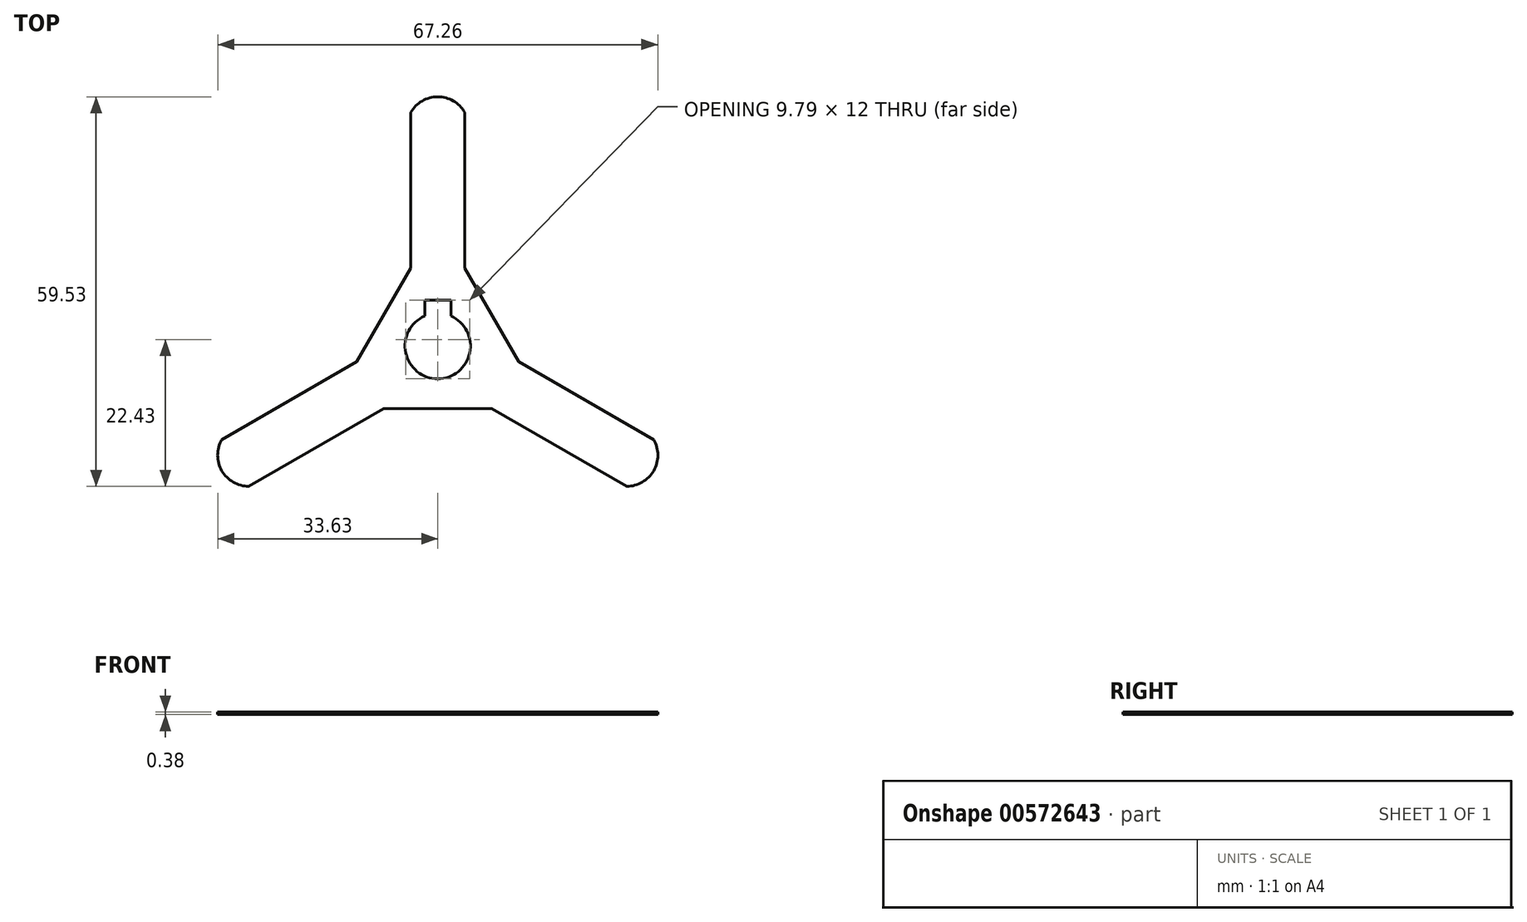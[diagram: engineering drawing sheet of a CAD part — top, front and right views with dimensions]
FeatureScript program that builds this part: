
annotation { "Feature Type Name" : "Feature", "Feature Type Description" : "" }
export const myFeature = defineFeature(function(context is Context, id is Id, definition is map)
    precondition{}
    {
        {
            assignVariable(context, id + "F0", {"name" : "AT", "anyValue" : 3 / 8});
        }
        {
            var Q0;
            Q0=qCreatedBy(makeId("Top.planeOp"),FACE);
            var sketch = newSketch(context, id + "F1", { "sketchPlane" : qUnion([Q0])});
            skCircle(sketch, "E0.cCircle", {"center": v(0, 0) * mm, "radius": 42.86 * mm, "construction": true});
            skLineSegment(sketch, "E0.0", {"start": v(4.12, 35.72) * mm, "end": v(33, -14.29) * mm});
            skLineSegment(sketch, "E0.1", {"start": v(28.87, -21.43) * mm, "end": v(-28.87, -21.43) * mm});
            skLineSegment(sketch, "E0.2", {"start": v(-33, -14.29) * mm, "end": v(-4.12, 35.72) * mm});
            skPoint(sketch, "E1.visualSharp", {"position": v(0, 42.86) * mm});
            skArc(sketch, "E1.filletArc", {"start": v(4.12, 35.72) * mm, "mid": v(0, 38.1) * mm, "end": v(-4.12, 35.72) * mm});
            skPoint(sketch, "E2.visualSharp", {"position": v(37.12, -21.43) * mm});
            skArc(sketch, "E2.filletArc", {"start": v(28.87, -21.43) * mm, "mid": v(33, -19.05) * mm, "end": v(33, -14.29) * mm});
            skPoint(sketch, "E3.visualSharp", {"position": v(-37.12, -21.43) * mm});
            skArc(sketch, "E3.filletArc", {"start": v(-33, -14.29) * mm, "mid": v(-33, -19.05) * mm, "end": v(-28.87, -21.43) * mm});
            skPoint(sketch, "E4", {"position": v(-8.25, 0) * mm});
            skPoint(sketch, "E5", {"position": v(8.25, 0) * mm});
            skPoint(sketch, "E6", {"position": v(-4.12, -7.14) * mm});
            skPoint(sketch, "E7", {"position": v(4.12, -7.14) * mm});
            skPoint(sketch, "E8", {"position": v(4.12, 7.14) * mm});
            skPoint(sketch, "E9", {"position": v(-4.12, 7.14) * mm});
            skLineSegment(sketch, "E10", {"start": v(-28.87, -21.43) * mm, "end": v(-4.12, -7.14) * mm});
            skLineSegment(sketch, "E11", {"start": v(-33, -14.29) * mm, "end": v(-8.25, 0) * mm});
            skLineSegment(sketch, "E12", {"start": v(-4.12, 35.72) * mm, "end": v(-4.12, 7.14) * mm});
            skLineSegment(sketch, "E13", {"start": v(4.12, 7.14) * mm, "end": v(4.12, 35.72) * mm});
            skLineSegment(sketch, "E14", {"start": v(8.25, 0) * mm, "end": v(33, -14.29) * mm});
            skLineSegment(sketch, "E15", {"start": v(28.87, -21.43) * mm, "end": v(4.12, -7.14) * mm});
            skLineSegment(sketch, "E16", {"start": v(4.12, -7.14) * mm, "end": v(-4.12, -7.14) * mm});
            skLineSegment(sketch, "E17", {"start": v(-8.25, 0) * mm, "end": v(-4.12, 7.14) * mm});
            skLineSegment(sketch, "E18", {"start": v(4.12, 7.14) * mm, "end": v(8.25, 0) * mm});
            skCircle(sketch, "E19", {"center": v(0, 0) * mm, "radius": 5 * mm});
            skLineSegment(sketch, "E20", {"start": v(0, 5) * mm, "end": v(0, 3) * mm});
            skLineSegment(sketch, "E21", {"start": v(0, 3) * mm, "end": v(2, 3) * mm});
            skLineSegment(sketch, "E22", {"start": v(0, 3) * mm, "end": v(-2, 3) * mm});
            skLineSegment(sketch, "E23", {"start": v(-2, 3) * mm, "end": v(-2, 7) * mm});
            skLineSegment(sketch, "E24", {"start": v(-2, 7) * mm, "end": v(2, 7) * mm});
            skLineSegment(sketch, "E25", {"start": v(2, 7) * mm, "end": v(2, 3) * mm});
            skPoint(sketch, "E26", {"position": v(0, 5) * mm});
            skLineSegment(sketch, "E27", {"start": v(-2, 7) * mm, "end": v(2, 3) * mm});
            skLineSegment(sketch, "E28", {"start": v(0, 0) * mm, "end": v(0, 19.05) * mm});
            skLineSegment(sketch, "E29", {"start": v(0, 0) * mm, "end": v(16.5, -9.52) * mm});
            skLineSegment(sketch, "E30", {"start": v(0, 0) * mm, "end": v(-16.5, -9.52) * mm});
            skLineSegment(sketch, "E31", {"start": v(-16.5, -9.52) * mm, "end": v(0, 19.05) * mm});
            skLineSegment(sketch, "E32", {"start": v(16.5, -9.53) * mm, "end": v(0, 19.05) * mm});
            skLineSegment(sketch, "E33", {"start": v(-16.5, -9.52) * mm, "end": v(16.5, -9.52) * mm});
            skSolve(sketch);
        }
        {
            var Q0;
            Q0=makeQuery(id+"F1.imprint","IMPRINT",FACE,{"disambiguationData":[TD([[makeQuery(id+"F1.imprint","IMPRINT",EDGE,{"derivedFrom":sQuery(id+"F1.wireOp",EDGE,"E1.filletArc")}),1.0]])]});
            var Q1;
            {var subQ5=sQuery(id+"F1.wireOp",EDGE,"E18");Q1=makeQuery(id+"F1.imprint","IMPRINT",FACE,{"disambiguationData":[TD([[makeQuery(id+"F1.imprint","IMPRINT",EDGE,{"derivedFrom":subQ5}),-1.0]])]});}
            var Q2;
            {var subQ5=sQuery(id+"F1.wireOp",EDGE,"E17");Q2=makeQuery(id+"F1.imprint","IMPRINT",FACE,{"disambiguationData":[TD([[makeQuery(id+"F1.imprint","IMPRINT",EDGE,{"derivedFrom":subQ5}),-1.0]])]});}
            var Q3;
            {var subQ5=sQuery(id+"F1.wireOp",EDGE,"E16");Q3=makeQuery(id+"F1.imprint","IMPRINT",FACE,{"disambiguationData":[TD([[makeQuery(id+"F1.imprint","IMPRINT",EDGE,{"derivedFrom":subQ5}),-1.0]])]});}
            var Q4;
            {var subQ6=sQuery(id+"F1.wireOp",EDGE,"E2.filletArc");Q4=makeQuery(id+"F1.imprint","IMPRINT",FACE,{"disambiguationData":[TD([[makeQuery(id+"F1.imprint","IMPRINT",EDGE,{"derivedFrom":subQ6}),1.0]])]});}
            var Q5;
            {var subQ5=sQuery(id+"F1.wireOp",EDGE,"E3.filletArc");Q5=makeQuery(id+"F1.imprint","IMPRINT",FACE,{"disambiguationData":[TD([[makeQuery(id+"F1.imprint","IMPRINT",EDGE,{"derivedFrom":subQ5}),1.0]])]});}
            var Q6;
            {var subQ0=sQuery(id+"F1.wireOp",EDGE,"E16");Q6=makeQuery(id+"F1.imprint","IMPRINT",FACE,{"disambiguationData":[TD([[makeQuery(id+"F1.imprint","IMPRINT",EDGE,{"derivedFrom":subQ0}),1.0]])]});}
            var Q7;
            {var subQ0=sQuery(id+"F1.wireOp",EDGE,"E18");Q7=makeQuery(id+"F1.imprint","IMPRINT",FACE,{"disambiguationData":[TD([[makeQuery(id+"F1.imprint","IMPRINT",EDGE,{"derivedFrom":subQ0}),1.0]])]});}
            var Q8;
            {var subQ0=sQuery(id+"F1.wireOp",EDGE,"E17");Q8=makeQuery(id+"F1.imprint","IMPRINT",FACE,{"disambiguationData":[TD([[makeQuery(id+"F1.imprint","IMPRINT",EDGE,{"derivedFrom":subQ0}),1.0]])]});}
            extrude(context, id + "F2", {"entities" : qUnion([Q0, Q1, Q2, Q3, Q4, Q5, Q6, Q7, Q8]), "depth" : (getVariable(context, 'AT')) * mm, "offsetDistance" : 25.4 * mm});
        }
    });
